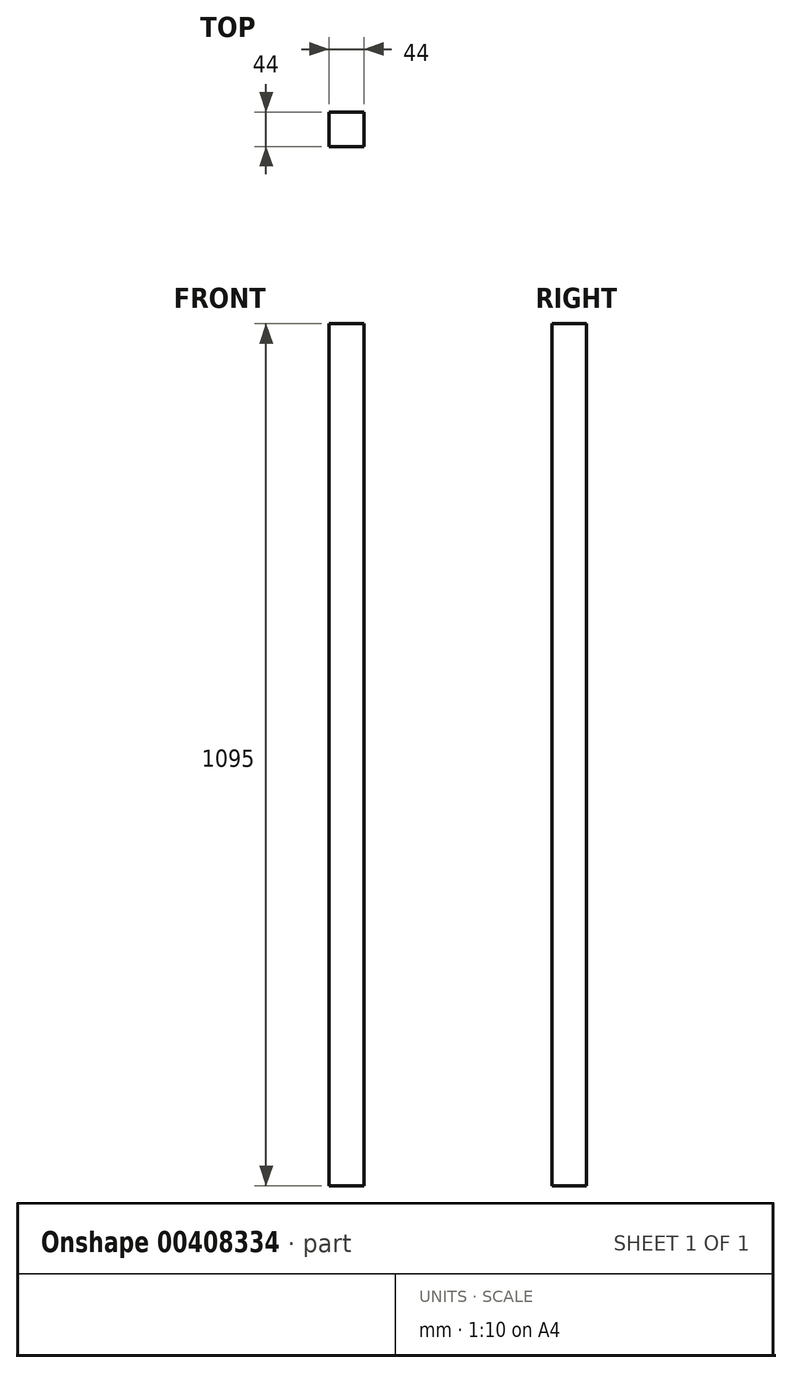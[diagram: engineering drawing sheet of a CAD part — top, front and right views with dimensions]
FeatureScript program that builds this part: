
annotation { "Feature Type Name" : "Feature", "Feature Type Description" : "" }
export const myFeature = defineFeature(function(context is Context, id is Id, definition is map)
    precondition{}
    {
        {
            var Q0;
            Q0=qCreatedBy(makeId("Top.planeOp"),FACE);
            var sketch = newSketch(context, id + "F0", { "sketchPlane" : qUnion([Q0])});
            skLineSegment(sketch, "E0.bottom", {"start": v(22, 22) * mm, "end": v(-22, 22) * mm});
            skLineSegment(sketch, "E0.top", {"start": v(22, -22) * mm, "end": v(-22, -22) * mm});
            skLineSegment(sketch, "E0.left", {"start": v(22, 22) * mm, "end": v(22, -22) * mm});
            skLineSegment(sketch, "E0.right", {"start": v(-22, 22) * mm, "end": v(-22, -22) * mm});
            skPoint(sketch, "E0.middle", {"position": v(0, 0) * mm});
            skSolve(sketch);
        }
        {
            var Q0;
            Q0=makeQuery(id+"F0.imprint","IMPRINT",FACE,{"disambiguationData":[TD([[makeQuery(id+"F0.imprint","IMPRINT",EDGE,{"derivedFrom":sQuery(id+"F0.wireOp",EDGE,"E0.bottom")}),1.0]])]});
            extrude(context, id + "F1", {"entities" : qUnion([Q0]), "depth" : (820 - 320 + 610 - 15) * mm});
        }
    });
